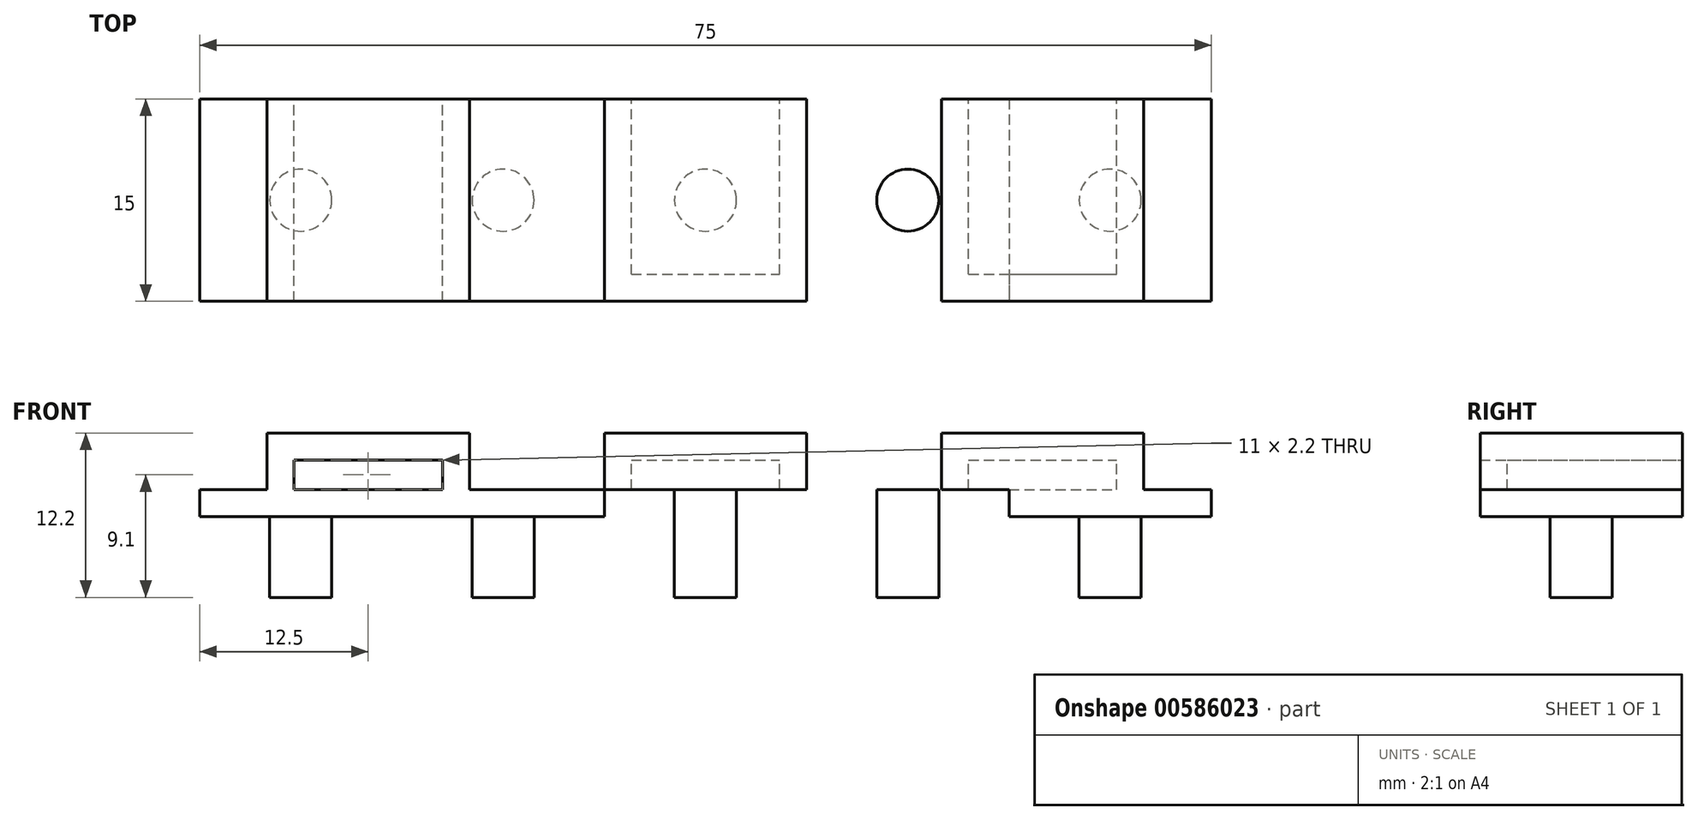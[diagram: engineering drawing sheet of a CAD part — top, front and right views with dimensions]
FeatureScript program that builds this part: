
annotation { "Feature Type Name" : "Feature", "Feature Type Description" : "" }
export const myFeature = defineFeature(function(context is Context, id is Id, definition is map)
    precondition{}
    {
        {
            var Q0;
            Q0=qCreatedBy(makeId("Top.planeOp"),FACE);
            var sketch = newSketch(context, id + "F0", { "sketchPlane" : qUnion([Q0])});
            skCircle(sketch, "E0", {"center": v(-30, 0) * mm, "radius": 2.3 * mm});
            skLineSegment(sketch, "E1.bottom", {"start": v(-37.5, 7.5) * mm, "end": v(-22.5, 7.5) * mm});
            skLineSegment(sketch, "E1.top", {"start": v(-37.5, -7.5) * mm, "end": v(-22.5, -7.5) * mm});
            skLineSegment(sketch, "E1.left", {"start": v(-37.5, 7.5) * mm, "end": v(-37.5, -7.5) * mm});
            skLineSegment(sketch, "E1.right", {"start": v(-22.5, 7.5) * mm, "end": v(-22.5, -7.5) * mm});
            skLineSegment(sketch, "E2.1.0.0", {"start": v(-7.5, 7.5) * mm, "end": v(-7.5, -7.5) * mm});
            skLineSegment(sketch, "E2.1.0.2", {"start": v(-22.5, 7.5) * mm, "end": v(-7.5, 7.5) * mm});
            skLineSegment(sketch, "E2.1.0.3", {"start": v(-22.5, -7.5) * mm, "end": v(-7.5, -7.5) * mm});
            skCircle(sketch, "E2.1.0.4", {"center": v(-15, 0) * mm, "radius": 2.3 * mm});
            skLineSegment(sketch, "E2.2.0.0", {"start": v(7.5, 7.5) * mm, "end": v(7.5, -7.5) * mm});
            skLineSegment(sketch, "E2.2.0.1", {"start": v(-7.5, 7.5) * mm, "end": v(-7.5, -7.5) * mm});
            skLineSegment(sketch, "E2.2.0.2", {"start": v(-7.5, 7.5) * mm, "end": v(7.5, 7.5) * mm});
            skLineSegment(sketch, "E2.2.0.3", {"start": v(-7.5, -7.5) * mm, "end": v(7.5, -7.5) * mm});
            skCircle(sketch, "E2.2.0.4", {"center": v(0, 0) * mm, "radius": 2.3 * mm});
            skLineSegment(sketch, "E2.3.0.0", {"start": v(22.5, 7.5) * mm, "end": v(22.5, -7.5) * mm});
            skLineSegment(sketch, "E2.3.0.1", {"start": v(7.5, 7.5) * mm, "end": v(7.5, -7.5) * mm});
            skLineSegment(sketch, "E2.3.0.2", {"start": v(7.5, 7.5) * mm, "end": v(22.5, 7.5) * mm});
            skLineSegment(sketch, "E2.3.0.3", {"start": v(7.5, -7.5) * mm, "end": v(22.5, -7.5) * mm});
            skCircle(sketch, "E2.3.0.4", {"center": v(15, 0) * mm, "radius": 2.3 * mm});
            skLineSegment(sketch, "E2.direction1", {"start": v(-37.5, -7.5) * mm, "end": v(-22.5, -7.5) * mm, "construction": true});
            skLineSegment(sketch, "E3.0.4.0", {"start": v(37.5, 7.5) * mm, "end": v(37.5, -7.5) * mm});
            skLineSegment(sketch, "E3.6.4.0", {"start": v(22.5, 7.5) * mm, "end": v(37.5, 7.5) * mm});
            skLineSegment(sketch, "E3.9.4.0", {"start": v(22.5, -7.5) * mm, "end": v(37.5, -7.5) * mm});
            skCircle(sketch, "E3.12.4.0", {"center": v(30, 0) * mm, "radius": 2.3 * mm});
            skSolve(sketch);
        }
        {
            var Q0;
            Q0=makeQuery(id+"F0.imprint","IMPRINT",FACE,{"disambiguationData":[TD([[makeQuery(id+"F0.imprint","IMPRINT",EDGE,{"derivedFrom":sQuery(id+"F0.wireOp",EDGE,"E0")}),-1.0]])]});
            var Q1;
            Q1=makeQuery(id+"F0.imprint","IMPRINT",FACE,{"disambiguationData":[TD([[makeQuery(id+"F0.imprint","IMPRINT",EDGE,{"derivedFrom":sQuery(id+"F0.wireOp",EDGE,"E1.right")}),1.0]])]});
            var Q2;
            Q2=makeQuery(id+"F0.imprint","IMPRINT",FACE,{"disambiguationData":[TD([[makeQuery(id+"F0.imprint","IMPRINT",EDGE,{"derivedFrom":sQuery(id+"F0.wireOp",EDGE,"E2.2.0.1")}),1.0]])]});
            var Q3;
            Q3=makeQuery(id+"F0.imprint","IMPRINT",FACE,{"disambiguationData":[TD([[makeQuery(id+"F0.imprint","IMPRINT",EDGE,{"derivedFrom":sQuery(id+"F0.wireOp",EDGE,"E2.3.0.1")}),1.0]])]});
            var Q4;
            Q4=makeQuery(id+"F0.imprint","IMPRINT",FACE,{"disambiguationData":[TD([[makeQuery(id+"F0.imprint","IMPRINT",EDGE,{"derivedFrom":sQuery(id+"F0.wireOp",EDGE,"E3.0.4.0")}),-1.0]])]});
            extrude(context, id + "F1", {"entities" : qUnion([Q0, Q1, Q2, Q3, Q4]), "oppositeDirection" : true, "depth" : 2 * mm, "offsetDistance" : 25 * mm});
        }
        {
            var Q0;
            Q0=makeQuery(id+"F0.imprint","IMPRINT",FACE,{"disambiguationData":[TD([[makeQuery(id+"F0.imprint","IMPRINT",EDGE,{"derivedFrom":sQuery(id+"F0.wireOp",EDGE,"HJVtsFcj-nnXf-v6pU-8xeC-anOBP0SdkL5j")}),1.0]])]});
            var Q1;
            Q1=makeQuery(id+"F0.imprint","IMPRINT",FACE,{"disambiguationData":[TD([[makeQuery(id+"F0.imprint","IMPRINT",EDGE,{"derivedFrom":sQuery(id+"F0.wireOp",EDGE,"E2.1.0.4")}),1.0]])]});
            var Q2;
            Q2=makeQuery(id+"F0.imprint","IMPRINT",FACE,{"disambiguationData":[TD([[makeQuery(id+"F0.imprint","IMPRINT",EDGE,{"derivedFrom":sQuery(id+"F0.wireOp",EDGE,"E0")}),1.0]])]});
            var Q3;
            Q3=makeQuery(id+"F0.imprint","IMPRINT",FACE,{"disambiguationData":[TD([[makeQuery(id+"F0.imprint","IMPRINT",EDGE,{"derivedFrom":sQuery(id+"F0.wireOp",EDGE,"E2.2.0.4")}),1.0]])]});
            var Q4;
            Q4=makeQuery(id+"F0.imprint","IMPRINT",FACE,{"disambiguationData":[TD([[makeQuery(id+"F0.imprint","IMPRINT",EDGE,{"derivedFrom":sQuery(id+"F0.wireOp",EDGE,"E2.3.0.4")}),1.0]])]});
            var Q5;
            Q5=makeQuery(id+"F0.imprint","IMPRINT",FACE,{"disambiguationData":[TD([[makeQuery(id+"F0.imprint","IMPRINT",EDGE,{"derivedFrom":sQuery(id+"F0.wireOp",EDGE,"E3.12.4.0")}),1.0]])]});
            extrude(context, id + "F2", {"entities" : qUnion([Q0, Q1, Q2, Q3, Q4, Q5]), "operationType" : NewBodyOperationType.ADD, "oppositeDirection" : true, "depth" : 8 * mm, "offsetDistance" : 25 * mm});
        }
        {
            var Q0;
            Q0=qCreatedBy(makeId("Front.planeOp"),FACE);
            var sketch = newSketch(context, id + "F3", { "sketchPlane" : qUnion([Q0])});
            skLineSegment(sketch, "E4.bottom", {"start": v(-32.5, 0) * mm, "end": v(-17.5, 0) * mm});
            skLineSegment(sketch, "E4.top", {"start": v(-32.5, 4.2) * mm, "end": v(-17.5, 4.2) * mm});
            skLineSegment(sketch, "E4.left", {"start": v(-32.5, 0) * mm, "end": v(-32.5, 4.2) * mm});
            skLineSegment(sketch, "E4.right", {"start": v(-17.5, 0) * mm, "end": v(-17.5, 4.2) * mm});
            skLineSegment(sketch, "E5.bottom", {"start": v(-30.5, 0) * mm, "end": v(-19.5, 0) * mm});
            skLineSegment(sketch, "E5.top", {"start": v(-30.5, 2.2) * mm, "end": v(-19.5, 2.2) * mm});
            skLineSegment(sketch, "E5.left", {"start": v(-30.5, 0) * mm, "end": v(-30.5, 2.2) * mm});
            skLineSegment(sketch, "E5.right", {"start": v(-19.5, 0) * mm, "end": v(-19.5, 2.2) * mm});
            skLineSegment(sketch, "E6.1.0.0", {"start": v(5.5, 0) * mm, "end": v(5.5, 2.2) * mm});
            skLineSegment(sketch, "E6.1.0.1", {"start": v(-7.5, 0) * mm, "end": v(7.5, 0) * mm});
            skLineSegment(sketch, "E6.1.0.2", {"start": v(-5.5, 0) * mm, "end": v(5.5, 0) * mm});
            skLineSegment(sketch, "E6.1.0.3", {"start": v(-7.5, 0) * mm, "end": v(-7.5, 4.2) * mm});
            skLineSegment(sketch, "E6.1.0.4", {"start": v(7.5, 0) * mm, "end": v(7.5, 4.2) * mm});
            skLineSegment(sketch, "E6.1.0.5", {"start": v(-5.5, 2.2) * mm, "end": v(5.5, 2.2) * mm});
            skLineSegment(sketch, "E6.1.0.6", {"start": v(-7.5, 4.2) * mm, "end": v(7.5, 4.2) * mm});
            skLineSegment(sketch, "E6.1.0.7", {"start": v(-5.5, 0) * mm, "end": v(-5.5, 2.2) * mm});
            skLineSegment(sketch, "E6.2.0.0", {"start": v(30.5, 0) * mm, "end": v(30.5, 2.2) * mm});
            skLineSegment(sketch, "E6.2.0.1", {"start": v(17.5, 0) * mm, "end": v(32.5, 0) * mm});
            skLineSegment(sketch, "E6.2.0.2", {"start": v(19.5, 0) * mm, "end": v(30.5, 0) * mm});
            skLineSegment(sketch, "E6.2.0.3", {"start": v(17.5, 0) * mm, "end": v(17.5, 4.2) * mm});
            skLineSegment(sketch, "E6.2.0.4", {"start": v(32.5, 0) * mm, "end": v(32.5, 4.2) * mm});
            skLineSegment(sketch, "E6.2.0.5", {"start": v(19.5, 2.2) * mm, "end": v(30.5, 2.2) * mm});
            skLineSegment(sketch, "E6.2.0.6", {"start": v(17.5, 4.2) * mm, "end": v(32.5, 4.2) * mm});
            skLineSegment(sketch, "E6.2.0.7", {"start": v(19.5, 0) * mm, "end": v(19.5, 2.2) * mm});
            skLineSegment(sketch, "E6.direction1", {"start": v(-32.5, 0) * mm, "end": v(-7.5, 0) * mm, "construction": true});
            skSolve(sketch);
        }
        {
            var Q0;
            Q0=makeQuery(id+"F3.imprint","IMPRINT",FACE,{"disambiguationData":[TD([[makeQuery(id+"F3.imprint","IMPRINT",EDGE,{"derivedFrom":sQuery(id+"F3.wireOp",EDGE,"E4.top")}),-1.0]])]});
            var Q1;
            {var subQ3=sQuery(id+"F3.wireOp",EDGE,"E6.1.0.0");Q1=makeQuery(id+"F3.imprint","IMPRINT",FACE,{"disambiguationData":[TD([[makeQuery(id+"F3.imprint","IMPRINT",EDGE,{"derivedFrom":subQ3}),-1.0]])]});}
            var Q2;
            {var subQ3=sQuery(id+"F3.wireOp",EDGE,"E6.2.0.0");Q2=makeQuery(id+"F3.imprint","IMPRINT",FACE,{"disambiguationData":[TD([[makeQuery(id+"F3.imprint","IMPRINT",EDGE,{"derivedFrom":subQ3}),-1.0]])]});}
            extrude(context, id + "F4", {"entities" : qUnion([Q0, Q1, Q2]), "operationType" : NewBodyOperationType.ADD, "endBound" : BoundingType.SYMMETRIC, "depth" : 15 * mm, "offsetDistance" : 25 * mm});
        }
        {
            var Q0;
            Q0=makeQuery(id+"F3.imprint","IMPRINT",FACE,{"disambiguationData":[TD([[makeQuery(id+"F3.imprint","IMPRINT",EDGE,{"derivedFrom":sQuery(id+"F3.wireOp",EDGE,"E5.bottom")}),1.0]])]});
            var Q1;
            Q1=makeQuery(id+"F3.imprint","IMPRINT",FACE,{"disambiguationData":[TD([[makeQuery(id+"F3.imprint","IMPRINT",EDGE,{"derivedFrom":sQuery(id+"F3.wireOp",EDGE,"E6.1.0.0")}),1.0]])]});
            var Q2;
            Q2=makeQuery(id+"F3.imprint","IMPRINT",FACE,{"disambiguationData":[TD([[makeQuery(id+"F3.imprint","IMPRINT",EDGE,{"derivedFrom":sQuery(id+"F3.wireOp",EDGE,"E6.2.0.0")}),1.0]])]});
            extrude(context, id + "F5", {"entities" : qUnion([Q0, Q1, Q2]), "operationType" : NewBodyOperationType.ADD, "depth" : 7.5 * mm, "offsetDistance" : 25 * mm, "hasSecondDirection" : true, "secondDirectionOppositeDirection" : false, "secondDirectionDepth" : 5.5 * mm});
        }
    });
